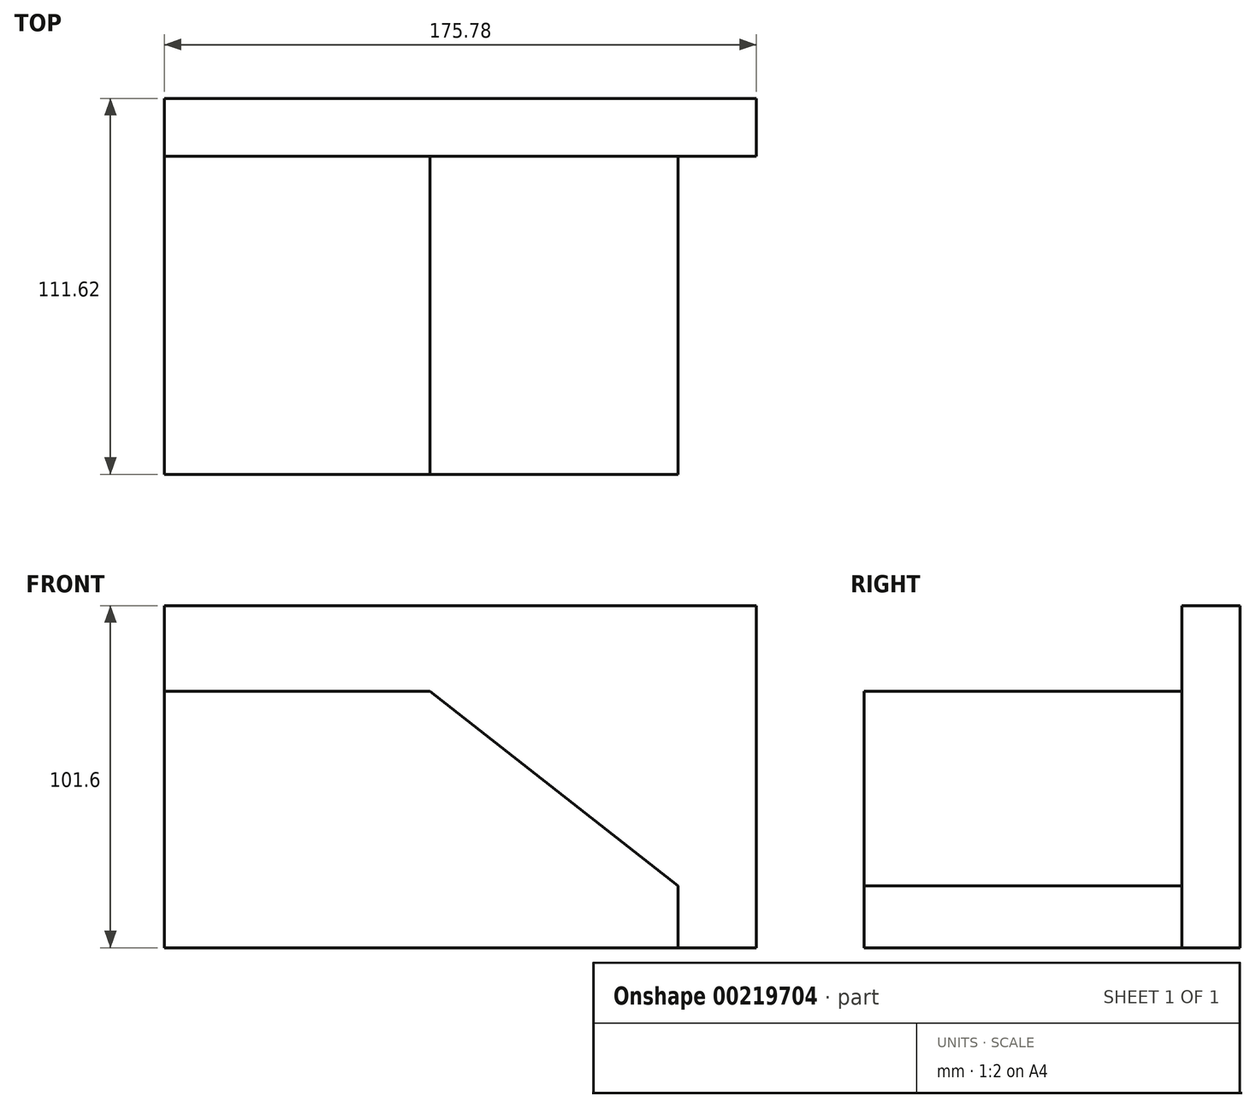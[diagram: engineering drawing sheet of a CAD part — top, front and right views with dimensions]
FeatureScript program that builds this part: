
annotation { "Feature Type Name" : "Feature", "Feature Type Description" : "" }
export const myFeature = defineFeature(function(context is Context, id is Id, definition is map)
    precondition{}
    {
        {
            var Q0;
            Q0=qCreatedBy(makeId("Top.planeOp"),FACE);
            var sketch = newSketch(context, id + "F0", { "sketchPlane" : qUnion([Q0])});
            skLineSegment(sketch, "E0.bottom", {"start": v(-76.25, 55.81) * mm, "end": v(76.25, 55.81) * mm});
            skLineSegment(sketch, "E0.top", {"start": v(-76.25, -55.81) * mm, "end": v(76.25, -55.81) * mm});
            skLineSegment(sketch, "E0.left", {"start": v(-76.25, 55.81) * mm, "end": v(-76.25, -55.81) * mm});
            skLineSegment(sketch, "E0.right", {"start": v(76.25, 55.81) * mm, "end": v(76.25, -55.81) * mm});
            skPoint(sketch, "E0.middle", {"position": v(0, 0) * mm});
            skSolve(sketch);
        }
        {
            var Q0;
            Q0=makeQuery(id+"F0.imprint","IMPRINT",FACE,{"disambiguationData":[TD([[makeQuery(id+"F0.imprint","IMPRINT",EDGE,{"derivedFrom":sQuery(id+"F0.wireOp",EDGE,"E0.bottom")}),-1.0]])]});
            var sketch = newSketch(context, id + "F1", { "sketchPlane" : qUnion([Q0])});
            skLineSegment(sketch, "E1.bottom", {"start": v(-76.25, 55.81) * mm, "end": v(99.53, 55.81) * mm});
            skLineSegment(sketch, "E1.top", {"start": v(-76.25, 38.58) * mm, "end": v(99.53, 38.58) * mm});
            skLineSegment(sketch, "E1.left", {"start": v(-76.25, 55.81) * mm, "end": v(-76.25, 38.58) * mm});
            skLineSegment(sketch, "E1.right", {"start": v(99.53, 55.81) * mm, "end": v(99.53, 38.58) * mm});
            skSolve(sketch);
        }
        {
            var Q0;
            Q0 = qSketchRegion(id + "F1", true);
            extrude(context, id + "F2", {"entities" : qUnion([Q0]), "depth" : 101.6 * mm});
        }
        {
            var Q0;
            Q0=makeQuery(id+"F0.imprint","IMPRINT",FACE,{"disambiguationData":[TD([[makeQuery(id+"F0.imprint","IMPRINT",EDGE,{"derivedFrom":sQuery(id+"F0.wireOp",EDGE,"E0.bottom")}),-1.0]])]});
            extrude(context, id + "F3", {"entities" : qUnion([Q0]), "operationType" : NewBodyOperationType.ADD, "depth" : 76.2 * mm});
        }
        {
            var Q0;
            Q0=makeQuery(id+"F2.opExtrude","SWEPT_FACE",FACE,{"disambiguationData":[OSD([sQuery(id+"F1.wireOp",EDGE,"E1.top")])]});
            var sketch = newSketch(context, id + "F4", { "sketchPlane" : qUnion([Q0])});
            skLineSegment(sketch, "E2", {"start": v(-29.63, 101.6) * mm, "end": v(99.53, 0) * mm});
            skLineSegment(sketch, "E3", {"start": v(99.53, 101.6) * mm, "end": v(-29.63, 101.6) * mm});
            skLineSegment(sketch, "E4", {"start": v(99.53, 101.6) * mm, "end": v(99.53, 0) * mm});
            skSolve(sketch);
        }
        {
            var Q0;
            Q0 = qSketchRegion(id + "F4", true);
            extrude(context, id + "F5", {"entities" : qUnion([Q0]), "operationType" : NewBodyOperationType.REMOVE, "endBound" : BoundingType.THROUGH_ALL, "depth" : 25.4 * mm});
        }
        {
            var Q0;
            Q0=makeQuery(id+"F5.boolean.opBoolean","MERGE",FACE,{"derivedFrom":[makeQuery(id+"F2.opExtrude","SWEPT_FACE",FACE,{"disambiguationData":[OSD([sQuery(id+"F1.wireOp",EDGE,"E1.top")])]}),makeQuery(id+"F5.opExtrude","CAP_FACE",FACE,{"disambiguationData":[OSD([sQuery(id+"F4.wireOp",EDGE,"E2"),sQuery(id+"F4.wireOp",EDGE,"E3"),sQuery(id+"F4.wireOp",EDGE,"E4")])],"isStart":true})]});
            var sketch = newSketch(context, id + "F6", { "sketchPlane" : qUnion([Q0])});
            skLineSegment(sketch, "E5", {"start": v(1.8, 101.6) * mm, "end": v(99.53, 0) * mm});
            skLineSegment(sketch, "E6", {"start": v(99.53, 0) * mm, "end": v(99.53, 101.6) * mm});
            skLineSegment(sketch, "E7", {"start": v(99.53, 101.6) * mm, "end": v(1.8, 101.6) * mm});
            skSolve(sketch);
        }
        {
            var Q0;
            Q0=makeQuery(id+"F6.imprint","IMPRINT",FACE,{"disambiguationData":[TD([[makeQuery(id+"F6.imprint","IMPRINT",EDGE,{"derivedFrom":sQuery(id+"F6.wireOp",EDGE,"E5")}),1.0]])]});
            extrude(context, id + "F7", {"entities" : qUnion([Q0]), "operationType" : NewBodyOperationType.REMOVE, "endBound" : BoundingType.THROUGH_ALL, "depth" : 25.4 * mm});
        }
    });
